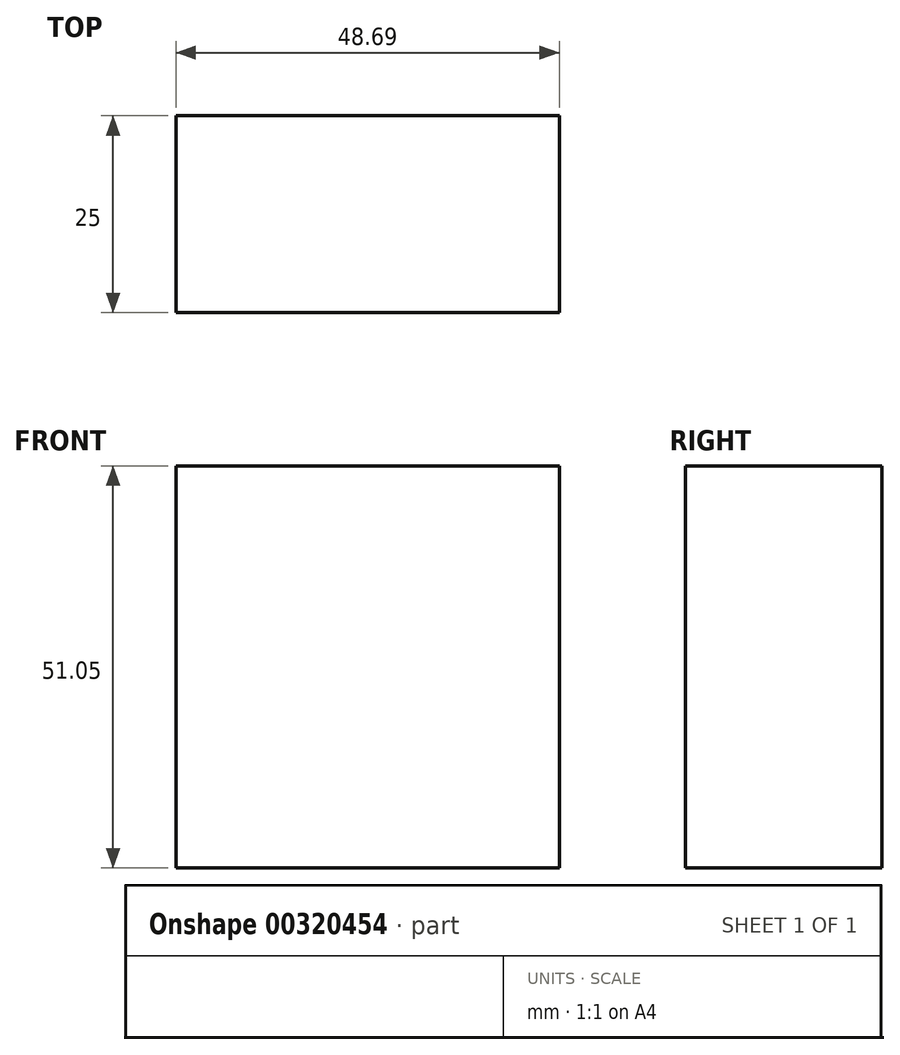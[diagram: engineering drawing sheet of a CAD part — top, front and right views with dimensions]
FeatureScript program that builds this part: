
annotation { "Feature Type Name" : "Feature", "Feature Type Description" : "" }
export const myFeature = defineFeature(function(context is Context, id is Id, definition is map)
    precondition{}
    {
        {
            var Q0;
            Q0=qCreatedBy(makeId("Front.planeOp"),FACE);
            var sketch = newSketch(context, id + "F0", { "sketchPlane" : qUnion([Q0])});
            skLineSegment(sketch, "E0.bottom", {"start": v(-90.88, 6.87) * mm, "end": v(-42.2, 6.87) * mm});
            skLineSegment(sketch, "E0.top", {"start": v(-90.88, 57.92) * mm, "end": v(-42.2, 57.92) * mm});
            skLineSegment(sketch, "E0.left", {"start": v(-90.88, 6.87) * mm, "end": v(-90.88, 57.92) * mm});
            skLineSegment(sketch, "E0.right", {"start": v(-42.2, 6.87) * mm, "end": v(-42.2, 57.92) * mm});
            skPoint(sketch, "E0.middle", {"position": v(-66.53, 32.4) * mm});
            skSolve(sketch);
        }
        {
            var Q0;
            Q0=makeQuery(id+"F0.imprint","IMPRINT",FACE,{"disambiguationData":[TD([[makeQuery(id+"F0.imprint","IMPRINT",EDGE,{"derivedFrom":sQuery(id+"F0.wireOp",EDGE,"E0.bottom")}),1.0]])]});
            extrude(context, id + "F1", {"entities" : qUnion([Q0]), "depth" : 25 * mm});
        }
    });
